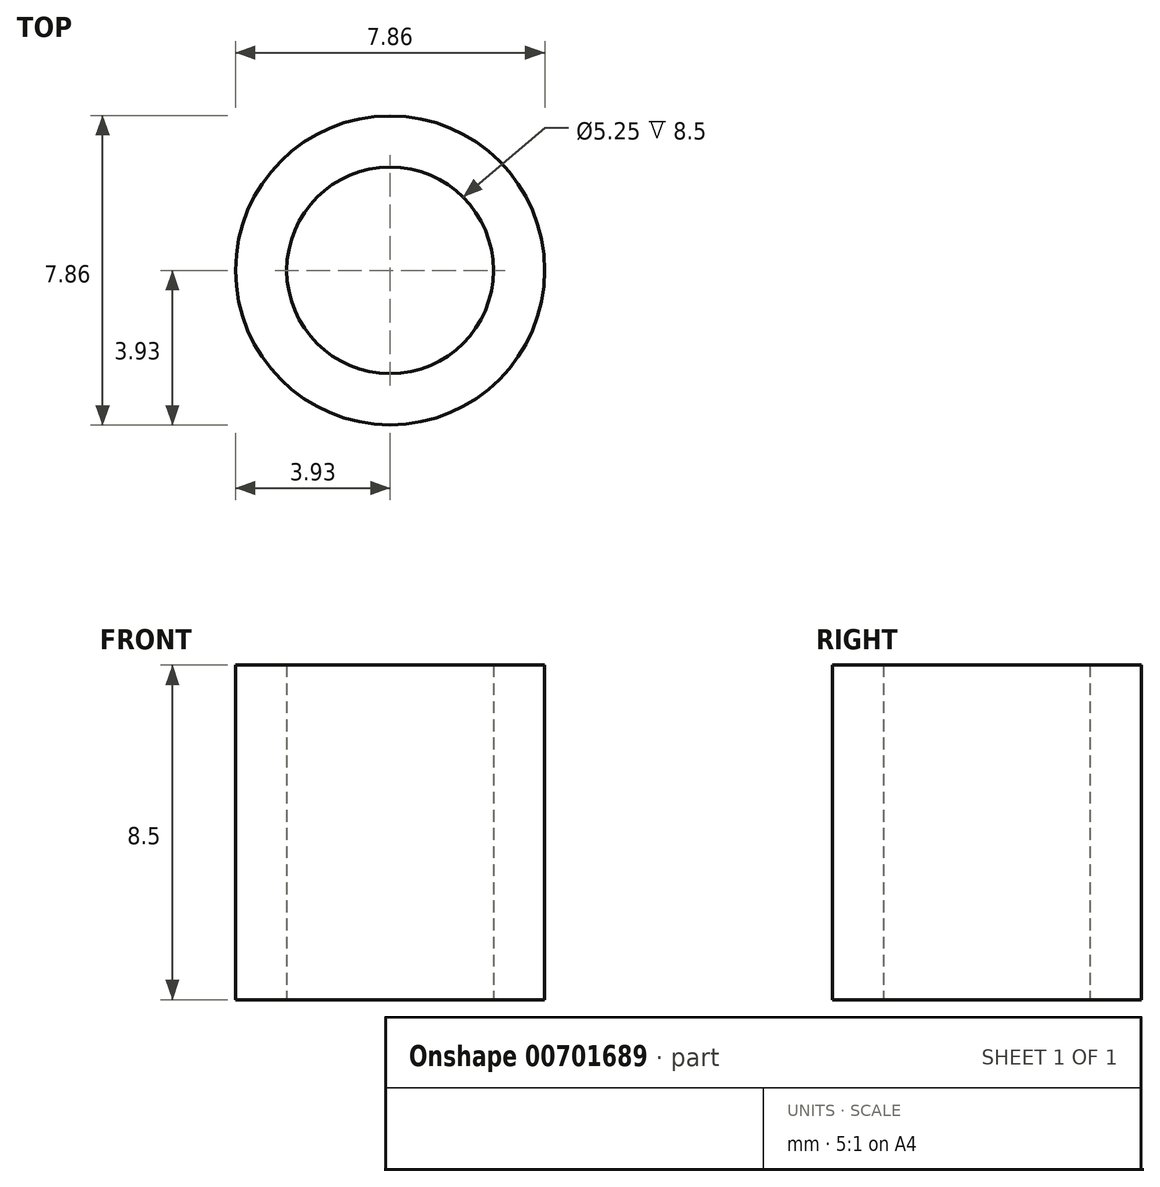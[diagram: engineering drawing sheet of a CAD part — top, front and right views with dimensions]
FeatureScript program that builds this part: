
annotation { "Feature Type Name" : "Feature", "Feature Type Description" : "" }
export const myFeature = defineFeature(function(context is Context, id is Id, definition is map)
    precondition{}
    {
        {
            var Q0;
            Q0=qCreatedBy(makeId("Top.planeOp"),FACE);
            var sketch = newSketch(context, id + "F0", { "sketchPlane" : qUnion([Q0])});
            skCircle(sketch, "E0", {"center": v(0, 0) * mm, "radius": 3.92 * mm});
            skCircle(sketch, "E1", {"center": v(0, 0) * mm, "radius": 2.62 * mm});
            skSolve(sketch);
        }
        {
            var Q0;
            Q0=makeQuery(id+"F0.imprint","IMPRINT",FACE,{"disambiguationData":[TD([[makeQuery(id+"F0.imprint","IMPRINT",EDGE,{"derivedFrom":sQuery(id+"F0.wireOp",EDGE,"E0")}),1.0]])]});
            extrude(context, id + "F1", {"entities" : qUnion([Q0]), "depth" : 8.5 * mm, "offsetDistance" : 25 * mm});
        }
    });
